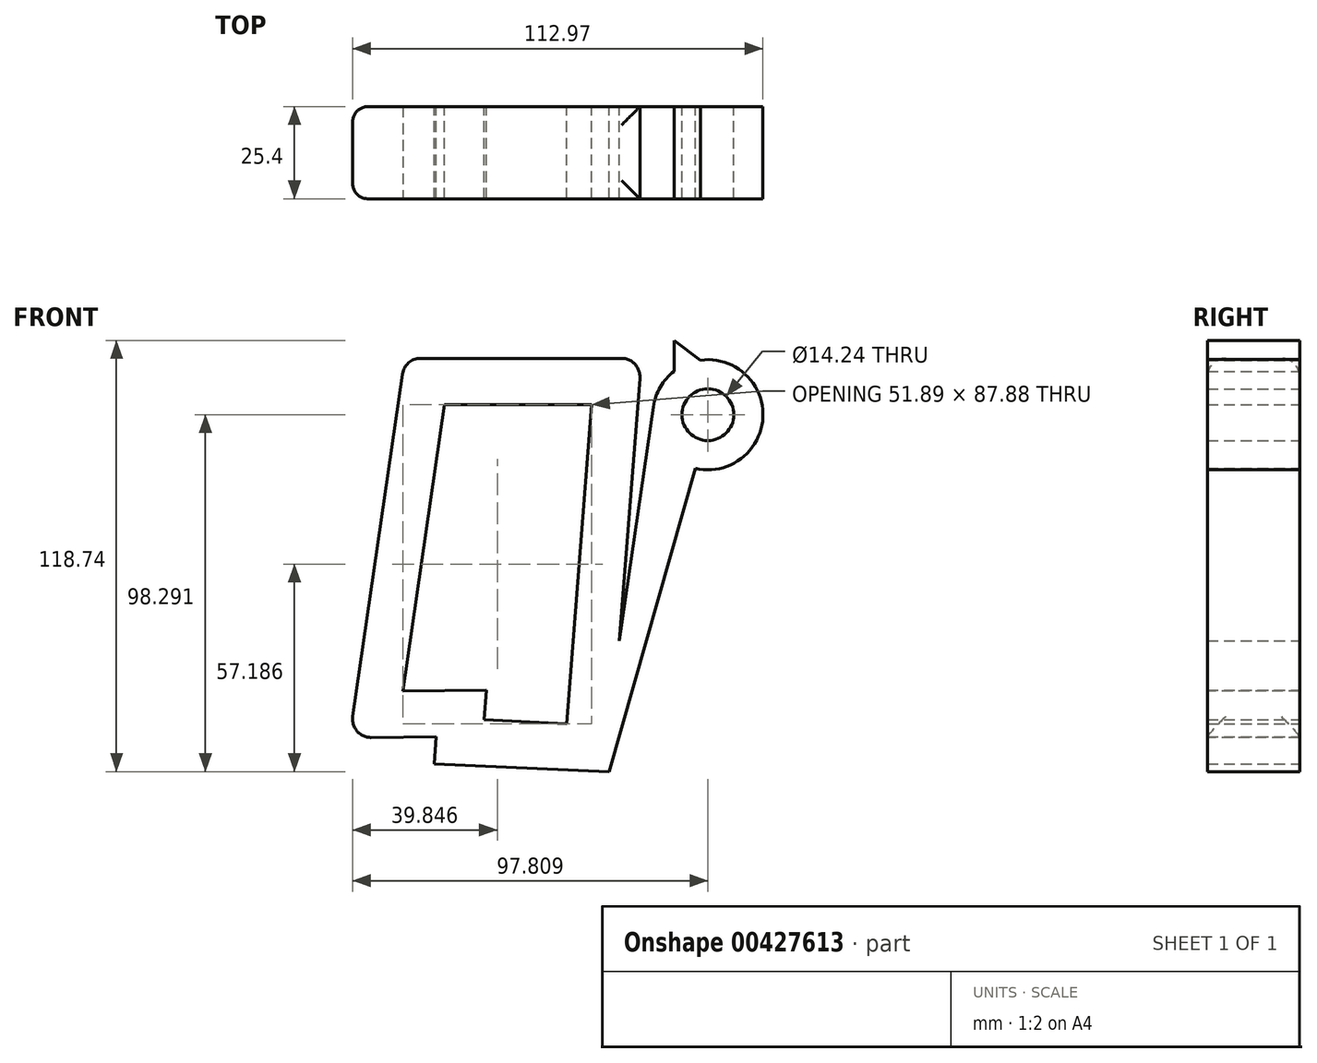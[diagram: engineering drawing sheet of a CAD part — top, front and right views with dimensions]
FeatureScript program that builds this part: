
annotation { "Feature Type Name" : "Feature", "Feature Type Description" : "" }
export const myFeature = defineFeature(function(context is Context, id is Id, definition is map)
    precondition{}
    {
        {
            var Q0;
            Q0=qCreatedBy(makeId("Front.planeOp"),FACE);
            var sketch = newSketch(context, id + "F0", { "sketchPlane" : qUnion([Q0])});
            skLineSegment(sketch, "E0", {"start": v(-36.53, 48.99) * mm, "end": v(-51.7, -55.47) * mm});
            skLineSegment(sketch, "E1", {"start": v(-36.53, 48.99) * mm, "end": v(-20.77, 35.63) * mm});
            skLineSegment(sketch, "E2", {"start": v(-20.77, 35.63) * mm, "end": v(-28.43, -62.66) * mm});
            skLineSegment(sketch, "E3", {"start": v(-51.7, -55.47) * mm, "end": v(-28.43, -62.66) * mm});
            skLineSegment(sketch, "E4", {"start": v(-20.77, 35.63) * mm, "end": v(31.9, 35.63) * mm});
            skLineSegment(sketch, "E5", {"start": v(-36.53, 48.99) * mm, "end": v(28.62, 48.99) * mm});
            skLineSegment(sketch, "E6", {"start": v(31.9, 35.63) * mm, "end": v(18.68, -55.47) * mm});
            skLineSegment(sketch, "E7", {"start": v(17.65, -54.86) * mm, "end": v(-51.7, -55.47) * mm});
            skLineSegment(sketch, "E8", {"start": v(28.62, 48.99) * mm, "end": v(19.74, -64.84) * mm});
            skLineSegment(sketch, "E9", {"start": v(-28.43, -62.66) * mm, "end": v(19.74, -64.84) * mm});
            skLineSegment(sketch, "E10", {"start": v(28.62, 48.99) * mm, "end": v(31.9, 35.63) * mm});
            skArc(sketch, "E11", {"start": v(31.9, 35.63) * mm, "mid": v(59.44, 41.98) * mm, "end": v(43.43, 18.7) * mm});
            skLineSegment(sketch, "E12", {"start": v(43.43, 18.7) * mm, "end": v(19.74, -64.84) * mm});
            skCircle(sketch, "E13", {"center": v(46.9, 33.45) * mm, "radius": 7.12 * mm});
            skLineSegment(sketch, "E14", {"start": v(44.86, 48.47) * mm, "end": v(37.58, 53.9) * mm});
            skLineSegment(sketch, "E15", {"start": v(37.58, 53.9) * mm, "end": v(37.58, 45.4) * mm});
            skLineSegment(sketch, "E16", {"start": v(50, 48.3) * mm, "end": v(42.26, 55.62) * mm});
            skLineSegment(sketch, "E17", {"start": v(42.26, 55.62) * mm, "end": v(44.86, 48.47) * mm});
            skSolve(sketch);
        }
        {
            var Q0;
            {var subQ0=sQuery(id+"F0.wireOp",EDGE,"E0");Q0=makeQuery(id+"F0.imprint","IMPRINT",FACE,{"disambiguationData":[TD([[makeQuery(id+"F0.imprint","IMPRINT",EDGE,{"derivedFrom":subQ0}),1.0]])]});}
            extrude(context, id + "F1", {"entities" : qUnion([Q0]), "endBound" : BoundingType.SYMMETRIC, "depth" : 25.4 * mm});
        }
        {
            var Q0;
            {var subQ0=sQuery(id+"F0.wireOp",EDGE,"E1");Q0=makeQuery(id+"F0.imprint","IMPRINT",FACE,{"disambiguationData":[TD([[makeQuery(id+"F0.imprint","IMPRINT",EDGE,{"derivedFrom":subQ0}),1.0]])]});}
            extrude(context, id + "F2", {"entities" : qUnion([Q0]), "operationType" : NewBodyOperationType.ADD, "endBound" : BoundingType.SYMMETRIC, "depth" : 25.4 * mm});
        }
        {
            var Q0;
            {var subQ6=sQuery(id+"F0.wireOp",EDGE,"E9");Q0=makeQuery(id+"F0.imprint","IMPRINT",FACE,{"disambiguationData":[TD([[makeQuery(id+"F0.imprint","IMPRINT",EDGE,{"derivedFrom":subQ6}),1.0]])]});}
            extrude(context, id + "F3", {"entities" : qUnion([Q0]), "operationType" : NewBodyOperationType.ADD, "endBound" : BoundingType.SYMMETRIC, "depth" : 25.4 * mm});
        }
        {
            var Q0;
            {var subQ5=sQuery(id+"F0.wireOp",EDGE,"E12");Q0=makeQuery(id+"F0.imprint","IMPRINT",FACE,{"disambiguationData":[TD([[makeQuery(id+"F0.imprint","IMPRINT",EDGE,{"derivedFrom":subQ5}),-1.0]])]});}
            extrude(context, id + "F4", {"entities" : qUnion([Q0]), "operationType" : NewBodyOperationType.ADD, "endBound" : BoundingType.SYMMETRIC, "depth" : 25.4 * mm});
        }
        {
            var Q0;
            {var subQ0=sQuery(id+"F0.wireOp",EDGE,"E14");Q0=makeQuery(id+"F0.imprint","IMPRINT",FACE,{"disambiguationData":[TD([[makeQuery(id+"F0.imprint","IMPRINT",EDGE,{"derivedFrom":subQ0}),1.0]])]});}
            extrude(context, id + "F5", {"entities" : qUnion([Q0]), "operationType" : NewBodyOperationType.ADD, "endBound" : BoundingType.SYMMETRIC, "depth" : 25.4 * mm});
        }
        {
            var Q0;
            Q0=makeQuery(id+"F2.opExtrude","CAP_EDGE",EDGE,{"disambiguationData":[OSD([sQuery(id+"F0.wireOp",EDGE,"E5")])],"isStart":false});
            var Q1;
            Q1=makeQuery(id+"F2.opExtrude","SWEPT_FACE",FACE,{"disambiguationData":[OSD([sQuery(id+"F0.wireOp",EDGE,"E5")])]});
            var Q2;
            Q2=makeQuery(id+"F1.opExtrude","SWEPT_FACE",FACE,{"disambiguationData":[OSD([sQuery(id+"F0.wireOp",EDGE,"E0")])]});
            fillet(context, id + "F6", {"entities" : qUnion([Q0, Q1, Q2]), "radius" : 5.08 * mm, "tangentPropagation" : true, "allowEdgeOverflow" : false});
        }
        {
            var Q0;
            {var subQ0=sQuery(id+"F0.wireOp",EDGE,"E11");var subQ1=sQuery(id+"F0.wireOp",EDGE,"E8");var subQ2=sQuery(id+"F0.wireOp",EDGE,"E4");var subQ3=sQuery(id+"F0.wireOp",EDGE,"E2");var subQ4=sQuery(id+"F0.wireOp",EDGE,"E1");Q0=makeQuery(id+"F5.boolean.opBoolean","MERGE",FACE,{"derivedFrom":[makeQuery(id+"F4.boolean.opBoolean","MERGE",FACE,{"derivedFrom":[makeQuery(id+"F3.boolean.opBoolean","MERGE",FACE,{"derivedFrom":[makeQuery(id+"F2.boolean.opBoolean","MERGE",FACE,{"derivedFrom":[makeQuery(id+"F1.opExtrude","CAP_FACE",FACE,{"disambiguationData":[OSD([sQuery(id+"F0.wireOp",EDGE,"E0"),subQ4,subQ3,sQuery(id+"F0.wireOp",EDGE,"E7")])],"isStart":false}),makeQuery(id+"F2.opExtrude","CAP_FACE",FACE,{"disambiguationData":[OSD([subQ4,subQ2,sQuery(id+"F0.wireOp",EDGE,"E5"),subQ1])],"isStart":false})]}),makeQuery(id+"F3.opExtrude","CAP_FACE",FACE,{"disambiguationData":[OSD([subQ3,subQ2,subQ1,sQuery(id+"F0.wireOp",EDGE,"E9")])],"isStart":false})]}),makeQuery(id+"F4.opExtrude","CAP_FACE",FACE,{"disambiguationData":[OSD([sQuery(id+"F0.wireOp",EDGE,"E6"),subQ1,subQ0,sQuery(id+"F0.wireOp",EDGE,"E12"),sQuery(id+"F0.wireOp",EDGE,"E13")])],"isStart":false})]}),makeQuery(id+"F5.opExtrude","CAP_FACE",FACE,{"disambiguationData":[OSD([subQ0,sQuery(id+"F0.wireOp",EDGE,"E14"),sQuery(id+"F0.wireOp",EDGE,"E15")])],"isStart":false})]});}
            var Q1;
            {var subQ0=sQuery(id+"F0.wireOp",EDGE,"E11");var subQ1=sQuery(id+"F0.wireOp",EDGE,"E8");var subQ2=sQuery(id+"F0.wireOp",EDGE,"E4");var subQ3=sQuery(id+"F0.wireOp",EDGE,"E2");var subQ4=sQuery(id+"F0.wireOp",EDGE,"E1");Q1=makeQuery(id+"F5.boolean.opBoolean","MERGE",FACE,{"derivedFrom":[makeQuery(id+"F4.boolean.opBoolean","MERGE",FACE,{"derivedFrom":[makeQuery(id+"F3.boolean.opBoolean","MERGE",FACE,{"derivedFrom":[makeQuery(id+"F2.boolean.opBoolean","MERGE",FACE,{"derivedFrom":[makeQuery(id+"F1.opExtrude","CAP_FACE",FACE,{"disambiguationData":[OSD([sQuery(id+"F0.wireOp",EDGE,"E0"),subQ4,subQ3,sQuery(id+"F0.wireOp",EDGE,"E7")])],"isStart":true}),makeQuery(id+"F2.opExtrude","CAP_FACE",FACE,{"disambiguationData":[OSD([subQ4,subQ2,sQuery(id+"F0.wireOp",EDGE,"E5"),subQ1])],"isStart":true})]}),makeQuery(id+"F3.opExtrude","CAP_FACE",FACE,{"disambiguationData":[OSD([subQ3,subQ2,subQ1,sQuery(id+"F0.wireOp",EDGE,"E9")])],"isStart":true})]}),makeQuery(id+"F4.opExtrude","CAP_FACE",FACE,{"disambiguationData":[OSD([sQuery(id+"F0.wireOp",EDGE,"E6"),subQ1,subQ0,sQuery(id+"F0.wireOp",EDGE,"E12"),sQuery(id+"F0.wireOp",EDGE,"E13")])],"isStart":true})]}),makeQuery(id+"F5.opExtrude","CAP_FACE",FACE,{"disambiguationData":[OSD([subQ0,sQuery(id+"F0.wireOp",EDGE,"E14"),sQuery(id+"F0.wireOp",EDGE,"E15")])],"isStart":true})]});}
            shell(context, id + "F7", {"entities" : qUnion([Q0, Q1]), "thickness" : 12.7 * mm});
        }
    });
